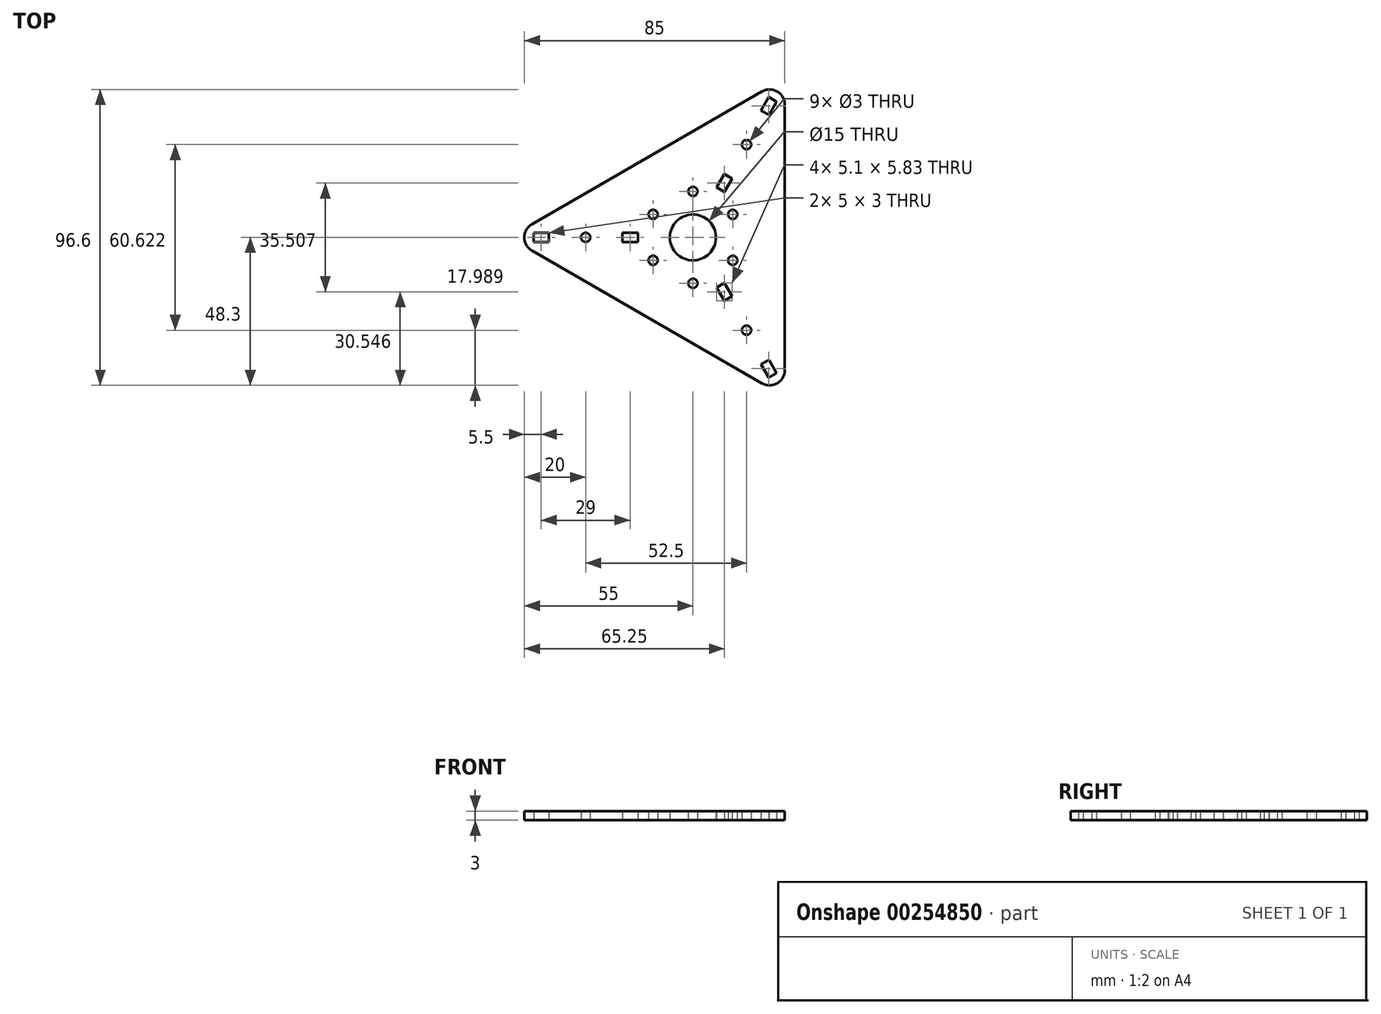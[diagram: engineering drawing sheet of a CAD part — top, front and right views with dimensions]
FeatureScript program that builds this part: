
annotation { "Feature Type Name" : "Feature", "Feature Type Description" : "" }
export const myFeature = defineFeature(function(context is Context, id is Id, definition is map)
    precondition{}
    {
        {
            var Q0;
            Q0=qCreatedBy(makeId("Top.planeOp"),FACE);
            var sketch = newSketch(context, id + "F0", { "sketchPlane" : qUnion([Q0])});
            skCircle(sketch, "E0.cCircle", {"center": v(0, 0) * mm, "radius": 60 * mm, "construction": true});
            skLineSegment(sketch, "E0.0", {"start": v(-52.5, 4.33) * mm, "end": v(22.5, 47.63) * mm});
            skLineSegment(sketch, "E0.1", {"start": v(30, 43.3) * mm, "end": v(30, -43.3) * mm});
            skLineSegment(sketch, "E0.2", {"start": v(22.5, -47.63) * mm, "end": v(-52.5, -4.33) * mm});
            skPoint(sketch, "E1.visualSharp", {"position": v(-60, 0) * mm});
            skArc(sketch, "E1.filletArc", {"start": v(-52.5, 4.33) * mm, "mid": v(-55, 0) * mm, "end": v(-52.5, -4.33) * mm});
            skPoint(sketch, "E2.visualSharp", {"position": v(30, 51.96) * mm});
            skArc(sketch, "E2.filletArc", {"start": v(30, 43.3) * mm, "mid": v(27.5, 47.63) * mm, "end": v(22.5, 47.63) * mm});
            skPoint(sketch, "E3.visualSharp", {"position": v(30, -51.96) * mm});
            skArc(sketch, "E3.filletArc", {"start": v(22.5, -47.63) * mm, "mid": v(27.5, -47.63) * mm, "end": v(30, -43.3) * mm});
            skLineSegment(sketch, "E4.bottom", {"start": v(-47, -1.5) * mm, "end": v(-52, -1.5) * mm});
            skLineSegment(sketch, "E4.top", {"start": v(-47, 1.5) * mm, "end": v(-52, 1.5) * mm});
            skLineSegment(sketch, "E4.left", {"start": v(-47, -1.5) * mm, "end": v(-47, 1.5) * mm});
            skLineSegment(sketch, "E4.right", {"start": v(-52, -1.5) * mm, "end": v(-52, 1.5) * mm});
            skPoint(sketch, "E4.middle", {"position": v(-49.5, 0) * mm});
            skLineSegment(sketch, "E5.bottom", {"start": v(-18, -1.5) * mm, "end": v(-23, -1.5) * mm});
            skLineSegment(sketch, "E5.top", {"start": v(-18, 1.5) * mm, "end": v(-23, 1.5) * mm});
            skLineSegment(sketch, "E5.left", {"start": v(-18, -1.5) * mm, "end": v(-18, 1.5) * mm});
            skLineSegment(sketch, "E5.right", {"start": v(-23, -1.5) * mm, "end": v(-23, 1.5) * mm});
            skPoint(sketch, "E5.middle", {"position": v(-20.5, 0) * mm});
            skPoint(sketch, "E6", {"position": v(-35, 0) * mm});
            skCircle(sketch, "E7", {"center": v(-35, 0) * mm, "radius": 1.5 * mm});
            skLineSegment(sketch, "E8.1.0", {"start": v(24.8, -39.95) * mm, "end": v(22.2, -41.45) * mm});
            skLineSegment(sketch, "E8.1.1", {"start": v(24.8, -39.95) * mm, "end": v(27.3, -44.28) * mm});
            skLineSegment(sketch, "E8.1.2", {"start": v(27.3, -44.28) * mm, "end": v(24.7, -45.78) * mm});
            skLineSegment(sketch, "E8.1.3", {"start": v(22.2, -41.45) * mm, "end": v(24.7, -45.78) * mm});
            skCircle(sketch, "E8.1.4", {"center": v(17.5, -30.31) * mm, "radius": 1.5 * mm});
            skLineSegment(sketch, "E8.1.5", {"start": v(7.7, -16.34) * mm, "end": v(10.2, -20.67) * mm});
            skLineSegment(sketch, "E8.1.6", {"start": v(12.8, -19.17) * mm, "end": v(10.2, -20.67) * mm});
            skLineSegment(sketch, "E8.1.7", {"start": v(10.3, -14.84) * mm, "end": v(7.7, -16.34) * mm});
            skLineSegment(sketch, "E8.1.8", {"start": v(10.3, -14.84) * mm, "end": v(12.8, -19.17) * mm});
            skLineSegment(sketch, "E8.2.0", {"start": v(22.2, 41.45) * mm, "end": v(24.8, 39.95) * mm});
            skLineSegment(sketch, "E8.2.1", {"start": v(22.2, 41.45) * mm, "end": v(24.7, 45.78) * mm});
            skLineSegment(sketch, "E8.2.2", {"start": v(24.7, 45.78) * mm, "end": v(27.3, 44.28) * mm});
            skLineSegment(sketch, "E8.2.3", {"start": v(24.8, 39.95) * mm, "end": v(27.3, 44.28) * mm});
            skCircle(sketch, "E8.2.4", {"center": v(17.5, 30.31) * mm, "radius": 1.5 * mm});
            skLineSegment(sketch, "E8.2.5", {"start": v(10.3, 14.84) * mm, "end": v(12.8, 19.17) * mm});
            skLineSegment(sketch, "E8.2.6", {"start": v(10.2, 20.67) * mm, "end": v(12.8, 19.17) * mm});
            skLineSegment(sketch, "E8.2.7", {"start": v(7.7, 16.34) * mm, "end": v(10.3, 14.84) * mm});
            skLineSegment(sketch, "E8.2.8", {"start": v(7.7, 16.34) * mm, "end": v(10.2, 20.67) * mm});
            skCircle(sketch, "E9", {"center": v(0, 0) * mm, "radius": 7.5 * mm});
            skCircle(sketch, "E10", {"center": v(-13, 7.5) * mm, "radius": 1.5 * mm});
            skLineSegment(sketch, "E11", {"start": v(0, 0) * mm, "end": v(-38.74, 22.37) * mm, "construction": true});
            skCircle(sketch, "E12.1.0", {"center": v(-13, -7.5) * mm, "radius": 1.5 * mm});
            skCircle(sketch, "E12.2.0", {"center": v(0, -15) * mm, "radius": 1.5 * mm});
            skCircle(sketch, "E12.3.0", {"center": v(13, -7.5) * mm, "radius": 1.5 * mm});
            skCircle(sketch, "E12.4.0", {"center": v(13, 7.5) * mm, "radius": 1.5 * mm});
            skCircle(sketch, "E12.5.0", {"center": v(0, 15) * mm, "radius": 1.5 * mm});
            skSolve(sketch);
        }
        {
            var Q0;
            Q0 = qSketchRegion(id + "F0", true);
            extrude(context, id + "F1", {"entities" : qUnion([Q0]), "depth" : 3 * mm, "symmetric" : true});
        }
    });
